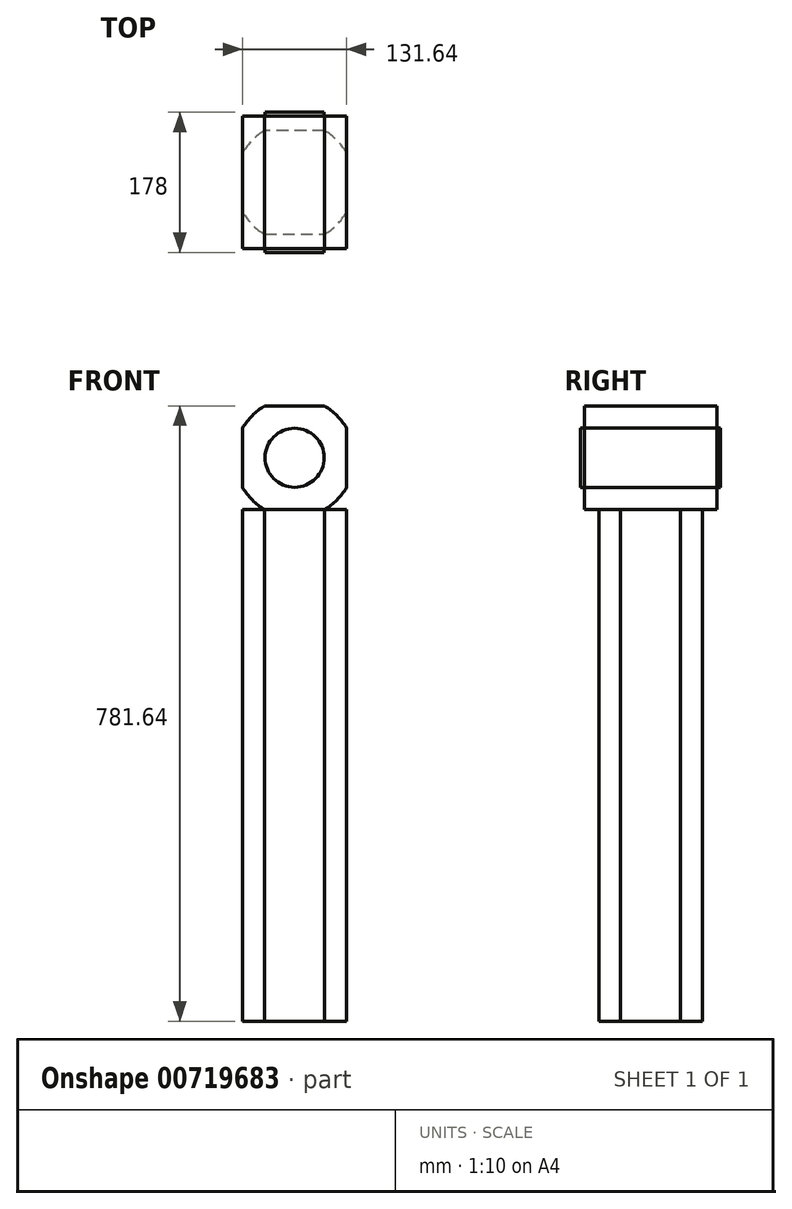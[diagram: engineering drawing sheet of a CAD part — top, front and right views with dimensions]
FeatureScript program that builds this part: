
annotation { "Feature Type Name" : "Feature", "Feature Type Description" : "" }
export const myFeature = defineFeature(function(context is Context, id is Id, definition is map)
    precondition{}
    {
        {
            var Q0;
            Q0=qCreatedBy(makeId("Front.planeOp"),FACE);
            var sketch = newSketch(context, id + "F0", { "sketchPlane" : qUnion([Q0])});
            skArc(sketch, "E0", {"start": v(-65.82, -38) * mm, "mid": v(-53.74, -53.74) * mm, "end": v(-38, -65.82) * mm});
            skLineSegment(sketch, "E1", {"start": v(0, 0) * mm, "end": v(-52.31, 90.6) * mm, "construction": true});
            skLineSegment(sketch, "E2", {"start": v(-52.31, 90.6) * mm, "end": v(0, 0) * mm, "construction": true});
            skLineSegment(sketch, "E3", {"start": v(0, 0) * mm, "end": v(-94.2, 54.39) * mm, "construction": true});
            skLineSegment(sketch, "E4", {"start": v(-65.82, 38) * mm, "end": v(-65.82, -38) * mm});
            skLineSegment(sketch, "E5", {"start": v(-38, 65.82) * mm, "end": v(38, 65.82) * mm});
            skLineSegment(sketch, "E6", {"start": v(0, 0) * mm, "end": v(51.51, -89.22) * mm, "construction": true});
            skLineSegment(sketch, "E7", {"start": v(0, 0) * mm, "end": v(94.02, -54.28) * mm, "construction": true});
            skLineSegment(sketch, "E8", {"start": v(65.82, -38) * mm, "end": v(65.82, 38) * mm});
            skLineSegment(sketch, "E9", {"start": v(38, -65.82) * mm, "end": v(-38, -65.82) * mm});
            skArc(sketch, "E10.trimOffspring", {"start": v(-38, 65.82) * mm, "mid": v(-53.74, 53.74) * mm, "end": v(-65.82, 38) * mm});
            skArc(sketch, "E11.trimOffspring", {"start": v(65.82, 38) * mm, "mid": v(53.74, 53.74) * mm, "end": v(38, 65.82) * mm});
            skArc(sketch, "E12.trimOffspring", {"start": v(38, -65.82) * mm, "mid": v(53.74, -53.74) * mm, "end": v(65.82, -38) * mm});
            skCircle(sketch, "E13", {"center": v(0, 0) * mm, "radius": 37.5 * mm});
            skSolve(sketch);
        }
        {
            var Q0;
            Q0 = qSketchRegion(id + "F0", true);
            var Q1;
            Q1=makeQuery(id+"F0.imprint","IMPRINT",FACE,{"disambiguationData":[TD([[makeQuery(id+"F0.imprint","IMPRINT",EDGE,{"derivedFrom":sQuery(id+"F0.wireOp",EDGE,"E13")}),1.0]])]});
            extrude(context, id + "F1", {"entities" : qUnion([Q0, Q1]), "depth" : 84 * mm, "offsetDistance" : 25 * mm, "hasSecondDirection" : true, "secondDirectionOppositeDirection" : true, "secondDirectionDepth" : 84 * mm});
        }
        {
            var Q0;
            Q0=makeQuery(id+"F0.imprint","IMPRINT",FACE,{"disambiguationData":[TD([[makeQuery(id+"F0.imprint","IMPRINT",EDGE,{"derivedFrom":sQuery(id+"F0.wireOp",EDGE,"E13")}),1.0]])]});
            extrude(context, id + "F2", {"entities" : qUnion([Q0]), "operationType" : NewBodyOperationType.ADD, "depth" : (178 / 2) * mm, "offsetDistance" : 25 * mm, "hasSecondDirection" : true, "secondDirectionOppositeDirection" : true, "secondDirectionDepth" : (178 / 2) * mm});
        }
        {
            var Q0;
            Q0=makeQuery(id+"F1.opExtrude","SWEPT_FACE",FACE,{"disambiguationData":[OSD([sQuery(id+"F0.wireOp",EDGE,"E9")])]});
            var sketch = newSketch(context, id + "F3", { "sketchPlane" : qUnion([Q0])});
            skArc(sketch, "E14", {"start": v(-65.82, -38) * mm, "mid": v(-53.74, -53.74) * mm, "end": v(-38, -65.82) * mm});
            skLineSegment(sketch, "E15", {"start": v(0, 0) * mm, "end": v(-52.31, 90.6) * mm, "construction": true});
            skLineSegment(sketch, "E16", {"start": v(-52.31, 90.6) * mm, "end": v(0, 0) * mm, "construction": true});
            skLineSegment(sketch, "E17", {"start": v(0, 0) * mm, "end": v(-94.2, 54.39) * mm, "construction": true});
            skLineSegment(sketch, "E18", {"start": v(-65.82, 38) * mm, "end": v(-65.82, -38) * mm});
            skLineSegment(sketch, "E19", {"start": v(-38, 65.82) * mm, "end": v(38, 65.82) * mm});
            skLineSegment(sketch, "E20", {"start": v(0, 0) * mm, "end": v(51.51, -89.22) * mm, "construction": true});
            skLineSegment(sketch, "E21", {"start": v(0, 0) * mm, "end": v(94.02, -54.28) * mm, "construction": true});
            skLineSegment(sketch, "E22", {"start": v(65.82, -38) * mm, "end": v(65.82, 38) * mm});
            skLineSegment(sketch, "E23", {"start": v(38, -65.82) * mm, "end": v(-38, -65.82) * mm});
            skArc(sketch, "E24.trimOffspring", {"start": v(-38, 65.82) * mm, "mid": v(-53.74, 53.74) * mm, "end": v(-65.82, 38) * mm});
            skArc(sketch, "E25.trimOffspring", {"start": v(65.82, 38) * mm, "mid": v(53.74, 53.74) * mm, "end": v(38, 65.82) * mm});
            skArc(sketch, "E26.trimOffspring", {"start": v(38, -65.82) * mm, "mid": v(53.74, -53.74) * mm, "end": v(65.82, -38) * mm});
            skCircle(sketch, "E27", {"center": v(0, 0) * mm, "radius": 37.5 * mm});
            skSolve(sketch);
        }
        {
            var Q0;
            {var subQ0=sQuery(id+"F3.wireOp",EDGE,"E14");Q0=makeQuery(id+"F3.imprint","IMPRINT",FACE,{"disambiguationData":[TD([[makeQuery(id+"F3.imprint","IMPRINT",EDGE,{"derivedFrom":subQ0}),1.0]])]});}
            var Q1;
            Q1=makeQuery(id+"F3.imprint","IMPRINT",FACE,{"disambiguationData":[TD([[makeQuery(id+"F3.imprint","IMPRINT",EDGE,{"derivedFrom":sQuery(id+"F3.wireOp",EDGE,"E22")}),1.0]])]});
            var Q2;
            Q2=makeQuery(id+"F3.imprint","IMPRINT",FACE,{"disambiguationData":[TD([[makeQuery(id+"F3.imprint","IMPRINT",EDGE,{"derivedFrom":sQuery(id+"F3.wireOp",EDGE,"E27")}),1.0]])]});
            var Q3;
            {var subQ3=sQuery(id+"F3.wireOp",EDGE,"E19");Q3=makeQuery(id+"F3.imprint","IMPRINT",FACE,{"disambiguationData":[TD([[makeQuery(id+"F3.imprint","IMPRINT",EDGE,{"derivedFrom":subQ3}),-1.0]])]});}
            extrude(context, id + "F4", {"entities" : qUnion([Q0, Q1, Q2, Q3]), "operationType" : NewBodyOperationType.ADD, "depth" : 650 * mm, "offsetDistance" : 25 * mm});
        }
    });
